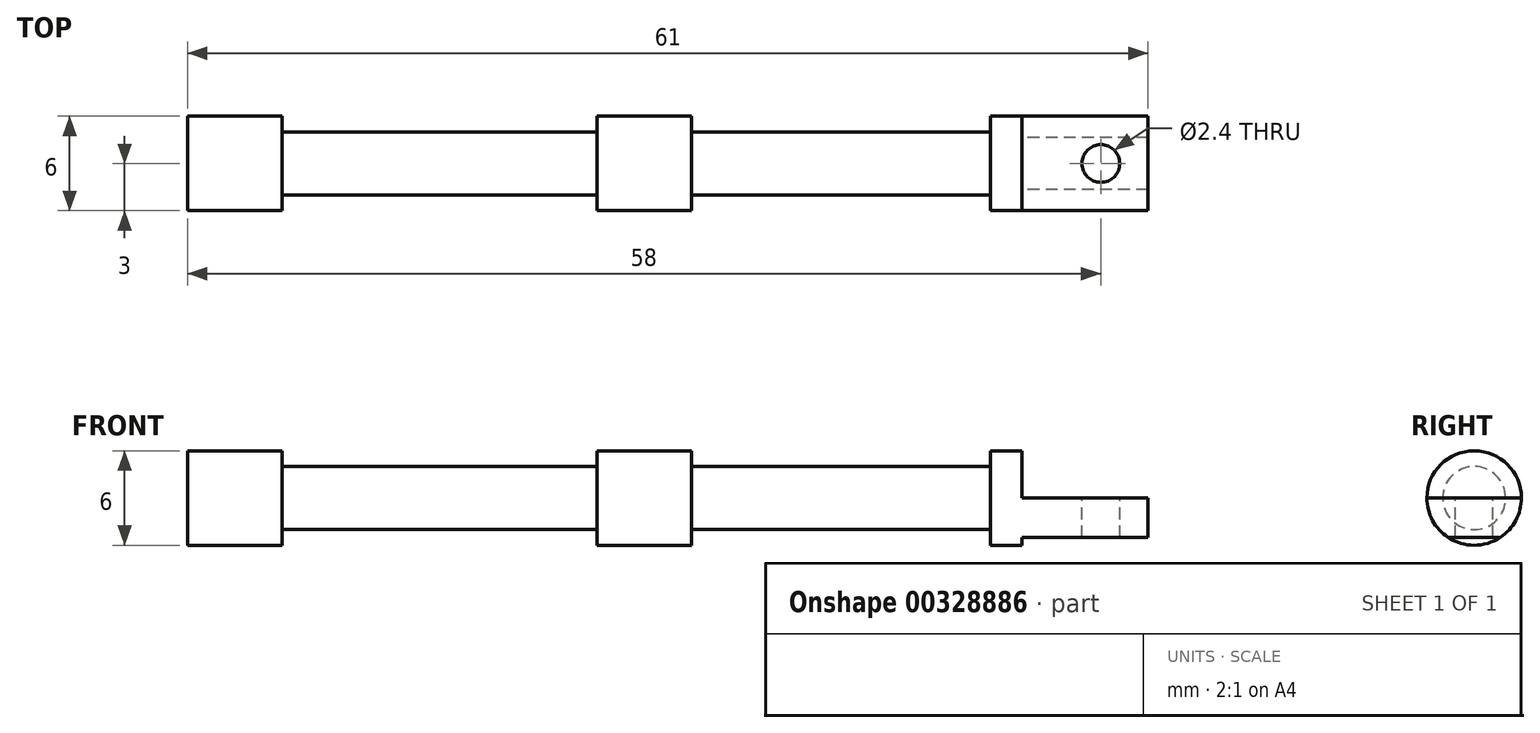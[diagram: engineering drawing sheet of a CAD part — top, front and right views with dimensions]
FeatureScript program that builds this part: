
annotation { "Feature Type Name" : "Feature", "Feature Type Description" : "" }
export const myFeature = defineFeature(function(context is Context, id is Id, definition is map)
    precondition{}
    {
        {
            var Q0;
            Q0=qCreatedBy(makeId("Front.planeOp"),FACE);
            var sketch = newSketch(context, id + "F0", { "sketchPlane" : qUnion([Q0])});
            skLineSegment(sketch, "E0", {"start": v(0, 0) * mm, "end": v(0, 3) * mm});
            skLineSegment(sketch, "E1", {"start": v(0, 3) * mm, "end": v(6, 3) * mm});
            skLineSegment(sketch, "E2", {"start": v(6, 3) * mm, "end": v(6, 2) * mm});
            skLineSegment(sketch, "E3", {"start": v(6, 2) * mm, "end": v(26, 2) * mm});
            skLineSegment(sketch, "E4", {"start": v(26, 2) * mm, "end": v(26, 3) * mm});
            skLineSegment(sketch, "E5", {"start": v(26, 3) * mm, "end": v(32, 3) * mm});
            skLineSegment(sketch, "E6", {"start": v(32, 3) * mm, "end": v(32, 2) * mm});
            skLineSegment(sketch, "E7", {"start": v(32, 2) * mm, "end": v(51, 2) * mm});
            skLineSegment(sketch, "E8", {"start": v(51, 2) * mm, "end": v(51, 3) * mm});
            skLineSegment(sketch, "E9", {"start": v(51, 3) * mm, "end": v(61, 3) * mm});
            skLineSegment(sketch, "E10", {"start": v(61, 3) * mm, "end": v(61, 0) * mm});
            skLineSegment(sketch, "E11", {"start": v(61, 0) * mm, "end": v(0, 0) * mm});
            skLineSegment(sketch, "E12", {"start": v(0, 0) * mm, "end": v(65.72, 0) * mm, "construction": true});
            skSolve(sketch);
        }
        {
            var Q0;
            Q0 = qSketchRegion(id + "F0", true);
            var Q1;
            Q1=sQuery(id+"F0.wireOp",EDGE,"E12");
            revolve(context, id + "F1", {"entities" : qUnion([Q0]), "axis" : qUnion([Q1]), "revolveType" : RevolveType.FULL});
        }
        {
            var Q0;
            Q0=qCreatedBy(makeId("Front.planeOp"),FACE);
            var sketch = newSketch(context, id + "F2", { "sketchPlane" : qUnion([Q0])});
            skLineSegment(sketch, "E13.bottom", {"start": v(53, 0) * mm, "end": v(64.29, 0) * mm});
            skLineSegment(sketch, "E13.top", {"start": v(53, 5.06) * mm, "end": v(64.29, 5.06) * mm});
            skLineSegment(sketch, "E13.left", {"start": v(53, 0) * mm, "end": v(53, 5.06) * mm});
            skLineSegment(sketch, "E13.right", {"start": v(64.29, 0) * mm, "end": v(64.29, 5.06) * mm});
            skLineSegment(sketch, "E14.bottom", {"start": v(53, -2.5) * mm, "end": v(64.29, -2.5) * mm});
            skLineSegment(sketch, "E14.top", {"start": v(53, -5.7) * mm, "end": v(64.29, -5.7) * mm});
            skLineSegment(sketch, "E14.left", {"start": v(53, -2.5) * mm, "end": v(53, -5.7) * mm});
            skLineSegment(sketch, "E14.right", {"start": v(64.29, -2.5) * mm, "end": v(64.29, -5.7) * mm});
            skSolve(sketch);
        }
        {
            var Q0;
            Q0 = qSketchRegion(id + "F2", true);
            extrude(context, id + "F3", {"entities" : qUnion([Q0]), "operationType" : NewBodyOperationType.REMOVE, "endBound" : BoundingType.THROUGH_ALL, "oppositeDirection" : true, "depth" : 25 * mm, "hasSecondDirection" : true, "secondDirectionBound" : SecondDirectionBoundingType.THROUGH_ALL, "secondDirectionOppositeDirection" : false, "secondDirectionDepth" : 25 * mm});
        }
        {
            var Q0;
            Q0=makeQuery(id+"F3.boolean.opBoolean","COPY",FACE,{"derivedFrom":makeQuery(id+"F3.opExtrude","SWEPT_FACE",FACE,{"disambiguationData":[OSD([sQuery(id+"F2.wireOp",EDGE,"E13.bottom")])]})});
            var sketch = newSketch(context, id + "F4", { "sketchPlane" : qUnion([Q0])});
            skCircle(sketch, "E15", {"center": v(58, 0) * mm, "radius": 1.2 * mm});
            skPoint(sketch, "E16", {"position": v(61, 0) * mm});
            skSolve(sketch);
        }
        {
            var Q0;
            Q0 = qSketchRegion(id + "F4", true);
            extrude(context, id + "F5", {"entities" : qUnion([Q0]), "operationType" : NewBodyOperationType.REMOVE, "endBound" : BoundingType.THROUGH_ALL, "oppositeDirection" : true, "depth" : 25 * mm});
        }
    });
